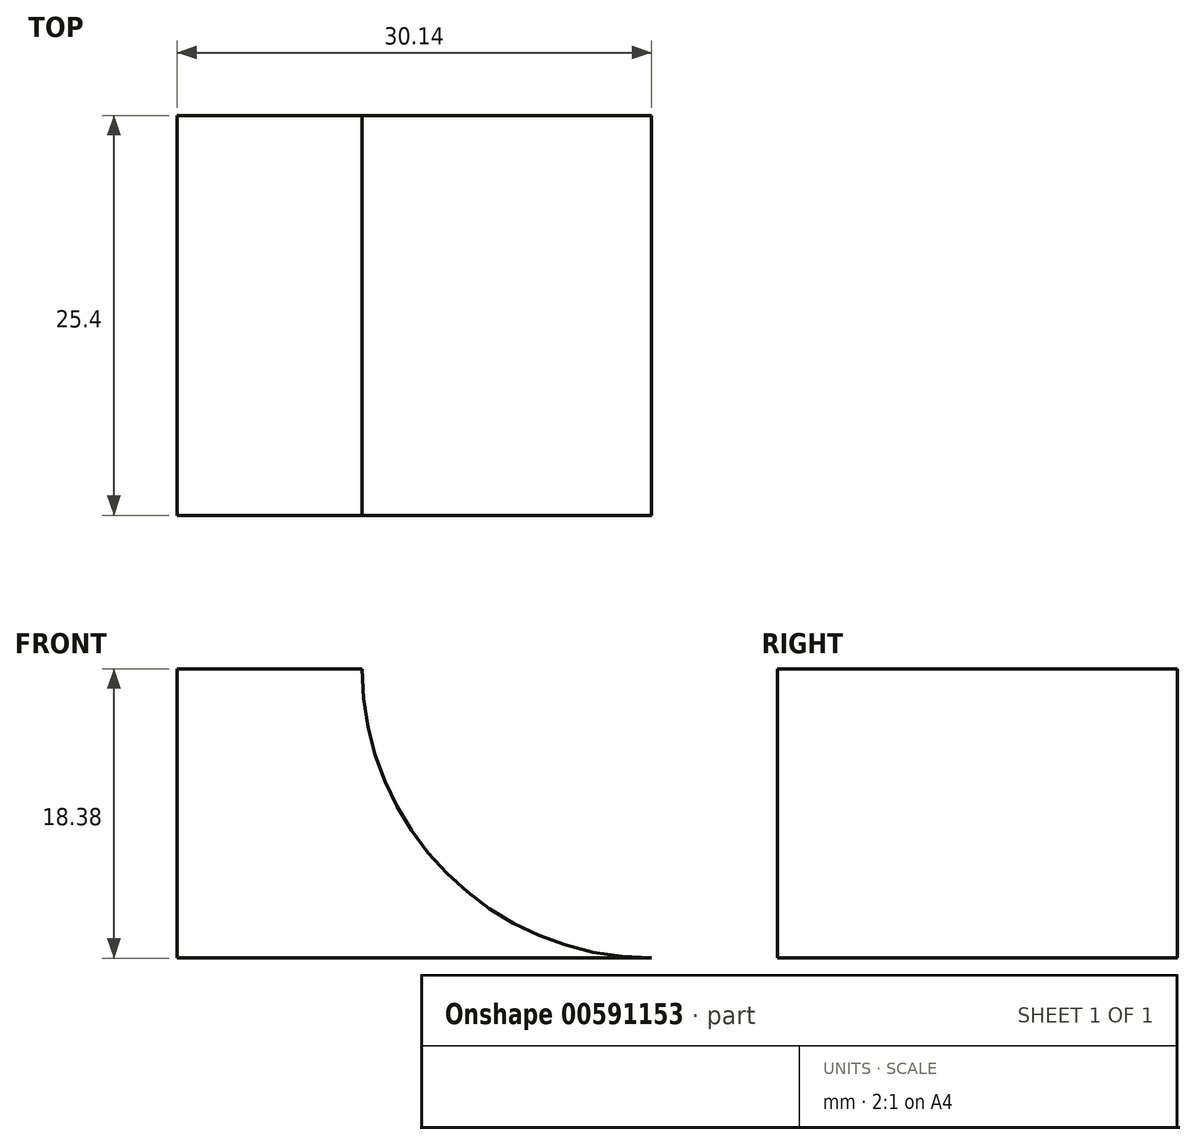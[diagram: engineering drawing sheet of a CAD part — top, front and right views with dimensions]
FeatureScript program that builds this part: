
annotation { "Feature Type Name" : "Feature", "Feature Type Description" : "" }
export const myFeature = defineFeature(function(context is Context, id is Id, definition is map)
    precondition{}
    {
        {
            var Q0;
            Q0=qCreatedBy(makeId("Front.planeOp"),FACE);
            var sketch = newSketch(context, id + "F0", { "sketchPlane" : qUnion([Q0])});
            skArc(sketch, "E0", {"start": v(-18.38, 0) * mm, "mid": v(-13, -13) * mm, "end": v(0, -18.38) * mm});
            skLineSegment(sketch, "E1.bottom", {"start": v(0, 0) * mm, "end": v(-30.14, 0) * mm});
            skLineSegment(sketch, "E1.top", {"start": v(0, -18.38) * mm, "end": v(-30.14, -18.38) * mm});
            skLineSegment(sketch, "E1.left", {"start": v(0, 0) * mm, "end": v(0, -18.38) * mm});
            skLineSegment(sketch, "E1.right", {"start": v(-30.14, 0) * mm, "end": v(-30.14, -18.38) * mm});
            skSolve(sketch);
        }
        {
            var Q0;
            {var subQ0=sQuery(id+"F0.wireOp",EDGE,"E0");Q0=makeQuery(id+"F0.imprint","IMPRINT",FACE,{"disambiguationData":[TD([[makeQuery(id+"F0.imprint","IMPRINT",EDGE,{"derivedFrom":subQ0}),-1.0]])]});}
            extrude(context, id + "F1", {"entities" : qUnion([Q0]), "depth" : 25.4 * mm, "offsetDistance" : 25.4 * mm});
        }
    });
